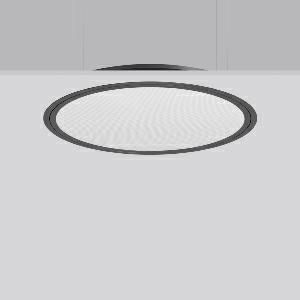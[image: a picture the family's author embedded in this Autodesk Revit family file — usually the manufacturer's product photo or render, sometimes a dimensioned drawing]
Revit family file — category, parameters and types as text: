
# Revit family: triona_round_e_312296_0031_12_02f3
name_source: partatom
category: Lighting Fixtures
units: mm (PartAtom-declared; Revit-internal decimal feet)

## family parameters
Cut with Voids When Loaded = No
Host = Face
Light Source = No
Part Type = Normal
Room Calculation Point = No
Round Connector Dimension = Use Diameter
Shared = No

## types (1)
- TRIONA round E (1 x LED Modul 830, 3750 lm, 3000)
    Apparent Load = 31 VA
    CIE Flux Codes = 58 86 97 100 100
    Color Rendering = 80
    Color Temperature = 3000
    Default Elevation = 1800 mm
    Description = Series: TRIONA round
Decorative round LED recessed surface luminaire. Cover made of sheet steel, powder-coated. Frame made of aluminium, powder-coated. Recessed ring: aluminium extrusion profile, powder coated. Light emission through a diffuser in plastic, opal/prismatic. Lightguide and diffuser made of non-yellowing plastic (PMMA). Lateral light emission (RZB SIDELITE technology) for above-average homogeneous light distribution. Suitable for installation in cavity ceilings. Tool-free mounting system thanks to the rocker arm mechanism (patent pending). Electronic ballast included. Very easy installation thanks to Plug+Play connection. Perfect for office areas (RUG < 19) and environments with computer screens in accordance with EN 12464-1. 
Colour: anthracite metallic (DB703)
Diameter: 725 mm
Height: 2 mm
Cut-out diameter: 702 mm
Recess height: 100 mm
Luminaire: recess height: 89 mm
Lamp: LED
Socket: without socket
Colour temperature: 3000K
Colour rendering index (CRI): 80
System power: 31 W
Rated luminous flux: 3750 lm
Luminous efficiency: 121 lm/W
Control gear: Converter, dimmable, DALI
Protection class: I
Type of protection: IP 40
    Height = 0 mm  [stored 0 ft]
    Lamp = 1 x LED Modul 830
    Lamp Light Flux = 3750 lm
    Lamp count = 1
    Length = 725 mm
    Lifetime = 50000 h
    Luminous efficacy = 121 lm/W
    Manufacturer = RZB
    ModVariant = No
    Model = 312296.0031.12
    Mounting Place = Ceiling
    Mounting Type = Recessed
    Number of Poles = 1
    OnlyDefault = Yes
    Power Factor = 1
    Product Name = TRIONA round E
    Product group = Recessed modular luminaires
    ProductGroupID = 406
    Protection Class = Protection class I
    Protection Degree = IP 20
    RLX_Detail_Level = 1
    RLX_Emergency_Light_Flux = 0 lm
    RLX_Emergency_Type = 0
    RLX_Emergency_Type_DB = No
    RlxData = <blob elided: 41205 chars, md5=32b49f59>
    Socket = socket
    Standby Power = 0 W
    System Light Flux = 3750 lm
    System Power = 31 W
    Type Comments = Product without accessories
    Type Image = 312296.0031.12.jpg
    URL = http://relux.com
    VarID = ---
    Voltage = 230 V
    Voltage Range = 220-240 V
    Weight = 0.00 kg
    Width = 0 mm  [stored 0 ft]

note: [stored X ft] marks values corroborated as IEEE doubles in the binary element streams (Revit-internal decimal feet)

## geometry (parser evidence)
native form markers: Blend x4, Sweep x10
no freeform markers — native parametric forms only
